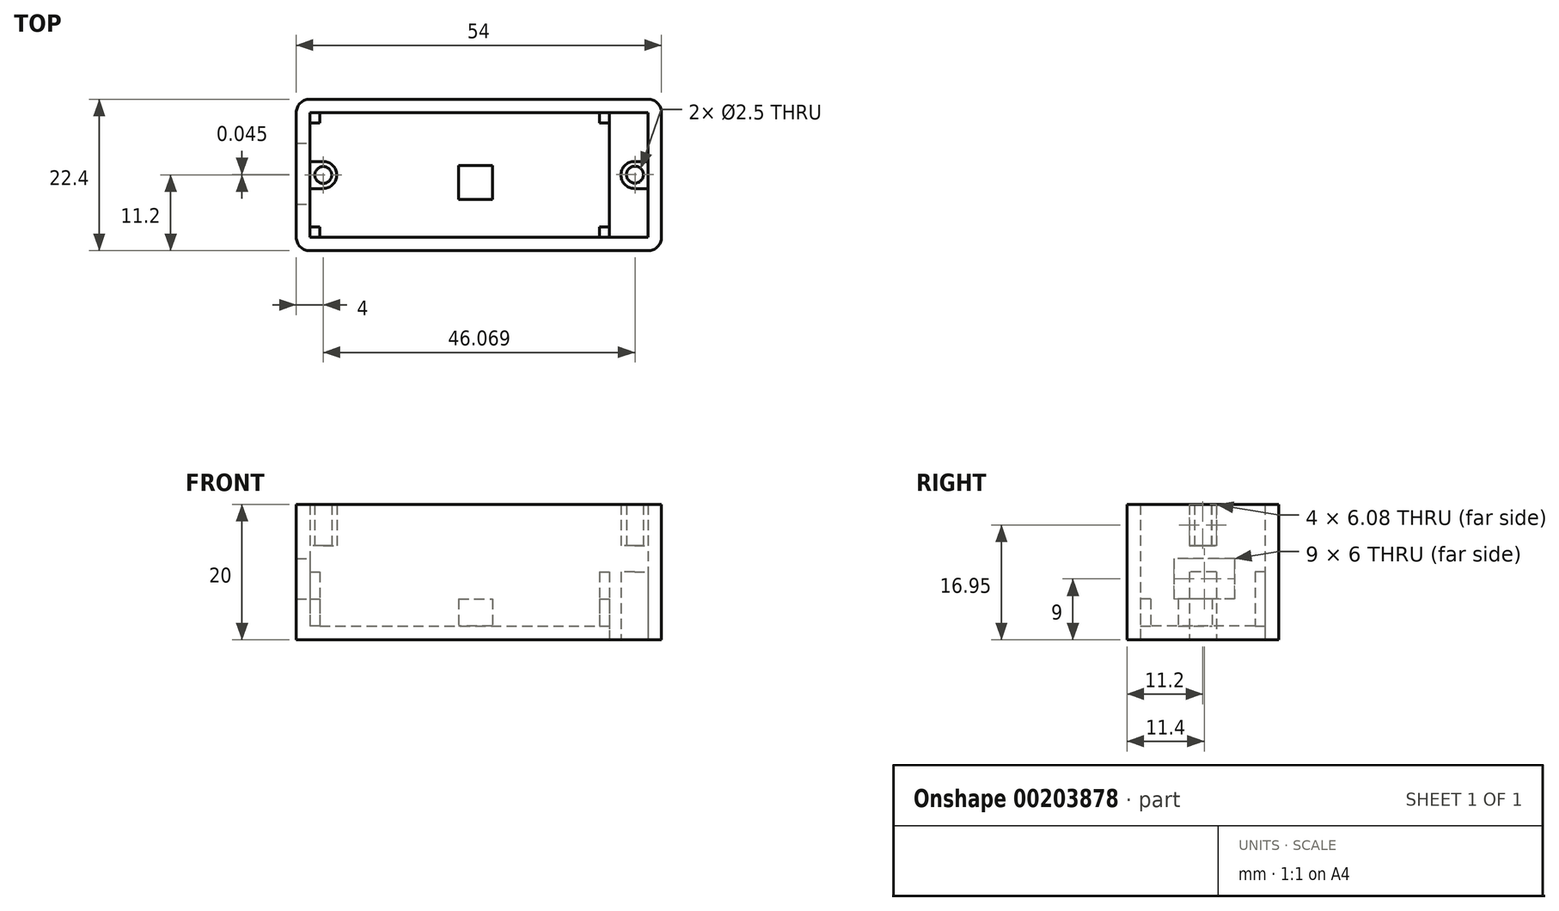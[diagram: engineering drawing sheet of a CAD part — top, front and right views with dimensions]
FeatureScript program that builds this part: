
annotation { "Feature Type Name" : "Feature", "Feature Type Description" : "" }
export const myFeature = defineFeature(function(context is Context, id is Id, definition is map)
    precondition{}
    {
        {
            var Q0;
            Q0=qCreatedBy(makeId("Top.planeOp"),FACE);
            var sketch = newSketch(context, id + "F0", { "sketchPlane" : qUnion([Q0])});
            skLineSegment(sketch, "E0.bottom", {"start": v(-31.58, 11.2) * mm, "end": v(22.42, 11.2) * mm});
            skLineSegment(sketch, "E0.top", {"start": v(-31.58, -11.2) * mm, "end": v(22.42, -11.2) * mm});
            skLineSegment(sketch, "E0.left", {"start": v(-31.58, 11.2) * mm, "end": v(-31.58, -11.2) * mm});
            skLineSegment(sketch, "E0.right", {"start": v(22.42, 11.2) * mm, "end": v(22.42, -11.2) * mm});
            skLineSegment(sketch, "E1.bottom", {"start": v(-29.58, 9.2) * mm, "end": v(20.42, 9.2) * mm});
            skLineSegment(sketch, "E1.top", {"start": v(-29.58, -9.2) * mm, "end": v(20.42, -9.2) * mm});
            skLineSegment(sketch, "E1.left", {"start": v(-29.58, 9.2) * mm, "end": v(-29.58, -9.2) * mm});
            skLineSegment(sketch, "E1.right", {"start": v(20.42, 9.2) * mm, "end": v(20.42, -9.2) * mm});
            skCircle(sketch, "E2", {"center": v(18.42, 0) * mm, "radius": 2 * mm});
            skCircle(sketch, "E3", {"center": v(-27.58, 0) * mm, "radius": 2 * mm});
            skLineSegment(sketch, "E4.bottom", {"start": v(-27.58, -2) * mm, "end": v(-29.58, -2) * mm});
            skLineSegment(sketch, "E4.top", {"start": v(-27.58, 2) * mm, "end": v(-29.58, 2) * mm});
            skLineSegment(sketch, "E4.left", {"start": v(-27.58, -2) * mm, "end": v(-27.58, 2) * mm});
            skLineSegment(sketch, "E4.right", {"start": v(-29.58, -2) * mm, "end": v(-29.58, 2) * mm});
            skLineSegment(sketch, "E5.bottom", {"start": v(18.42, 2) * mm, "end": v(20.42, 2) * mm});
            skLineSegment(sketch, "E5.top", {"start": v(18.42, -2) * mm, "end": v(20.42, -2) * mm});
            skLineSegment(sketch, "E5.left", {"start": v(18.42, 2) * mm, "end": v(18.42, -2) * mm});
            skLineSegment(sketch, "E5.right", {"start": v(20.42, 2) * mm, "end": v(20.42, -2) * mm});
            skCircle(sketch, "E6", {"center": v(-27.58, 0) * mm, "radius": 1.25 * mm});
            skCircle(sketch, "E7", {"center": v(18.49, 0.05) * mm, "radius": 1.25 * mm});
            skLineSegment(sketch, "E8.bottom", {"start": v(-29.58, 9.2) * mm, "end": v(14.72, 9.2) * mm});
            skLineSegment(sketch, "E8.top", {"start": v(-29.58, -9.2) * mm, "end": v(14.72, -9.2) * mm});
            skLineSegment(sketch, "E8.right", {"start": v(14.72, 9.2) * mm, "end": v(14.72, -9.2) * mm});
            skLineSegment(sketch, "E9.bottom", {"start": v(-7.58, 1.37) * mm, "end": v(-2.58, 1.37) * mm});
            skLineSegment(sketch, "E9.top", {"start": v(-7.58, -3.63) * mm, "end": v(-2.58, -3.63) * mm});
            skLineSegment(sketch, "E9.left", {"start": v(-7.58, 1.37) * mm, "end": v(-7.58, -3.63) * mm});
            skLineSegment(sketch, "E9.right", {"start": v(-2.58, 1.37) * mm, "end": v(-2.58, -3.63) * mm});
            skLineSegment(sketch, "E10.bottom", {"start": v(-28.08, 9.2) * mm, "end": v(-29.58, 9.2) * mm});
            skLineSegment(sketch, "E10.top", {"start": v(-28.08, 7.7) * mm, "end": v(-29.58, 7.7) * mm});
            skLineSegment(sketch, "E10.left", {"start": v(-28.08, 9.2) * mm, "end": v(-28.08, 7.7) * mm});
            skLineSegment(sketch, "E10.right", {"start": v(-29.58, 9.2) * mm, "end": v(-29.58, 7.7) * mm});
            skLineSegment(sketch, "E11.bottom", {"start": v(-29.58, -7.7) * mm, "end": v(-28.08, -7.7) * mm});
            skLineSegment(sketch, "E11.top", {"start": v(-29.58, -9.2) * mm, "end": v(-28.08, -9.2) * mm});
            skLineSegment(sketch, "E11.left", {"start": v(-29.58, -7.7) * mm, "end": v(-29.58, -9.2) * mm});
            skLineSegment(sketch, "E11.right", {"start": v(-28.08, -7.7) * mm, "end": v(-28.08, -9.2) * mm});
            skLineSegment(sketch, "E12.bottom", {"start": v(13.22, 9.2) * mm, "end": v(14.72, 9.2) * mm});
            skLineSegment(sketch, "E12.top", {"start": v(13.22, 7.7) * mm, "end": v(14.72, 7.7) * mm});
            skLineSegment(sketch, "E12.left", {"start": v(13.22, 9.2) * mm, "end": v(13.22, 7.7) * mm});
            skLineSegment(sketch, "E12.right", {"start": v(14.72, 9.2) * mm, "end": v(14.72, 7.7) * mm});
            skLineSegment(sketch, "E13.bottom", {"start": v(14.72, -7.7) * mm, "end": v(13.22, -7.7) * mm});
            skLineSegment(sketch, "E13.top", {"start": v(14.72, -9.2) * mm, "end": v(13.22, -9.2) * mm});
            skLineSegment(sketch, "E13.left", {"start": v(14.72, -7.7) * mm, "end": v(14.72, -9.2) * mm});
            skLineSegment(sketch, "E13.right", {"start": v(13.22, -7.7) * mm, "end": v(13.22, -9.2) * mm});
            skSolve(sketch);
        }
        {
            var Q0;
            Q0 = qSketchRegion(id + "F0", true);
            extrude(context, id + "F1", {"entities" : qUnion([Q0]), "depth" : 20 * mm});
        }
        {
            var Q0;
            Q0=makeQuery(id+"F0.imprint","IMPRINT",FACE,{"disambiguationData":[TD([[makeQuery(id+"F0.imprint","IMPRINT",EDGE,{"derivedFrom":sQuery(id+"F0.wireOp",EDGE,"E1.bottom")}),-1.0]])]});
            var Q1;
            {var subQ2=sQuery(id+"F0.wireOp",EDGE,"E4.bottom");Q1=makeQuery(id+"F0.imprint","IMPRINT",FACE,{"disambiguationData":[TD([[makeQuery(id+"F0.imprint","IMPRINT",EDGE,{"derivedFrom":subQ2}),1.0]])]});}
            var Q2;
            {var subQ0=sQuery(id+"F0.wireOp",EDGE,"E5.left");var subQ3=sQuery(id+"F0.wireOp",EDGE,"E7");var subQ5=makeQuery(id+"F0.imprint","INTERSECT",VERTEX,{"disambiguationData":[OD(0.0)],"derivedFrom":[subQ0,subQ3]});Q2=makeQuery(id+"F0.imprint","IMPRINT",FACE,{"disambiguationData":[TD([[makeQuery(id+"F0.imprint","IMPRINT",EDGE,{"disambiguationData":[TD([[subQ5,1.0]])],"derivedFrom":subQ3}),-1.0]])]});}
            var Q3;
            {var subQ0=sQuery(id+"F0.wireOp",EDGE,"E5.bottom");Q3=makeQuery(id+"F0.imprint","IMPRINT",FACE,{"disambiguationData":[TD([[makeQuery(id+"F0.imprint","IMPRINT",EDGE,{"derivedFrom":subQ0}),-1.0]])]});}
            var Q4;
            {var subQ0=sQuery(id+"F0.wireOp",EDGE,"E5.top");Q4=makeQuery(id+"F0.imprint","IMPRINT",FACE,{"disambiguationData":[TD([[makeQuery(id+"F0.imprint","IMPRINT",EDGE,{"derivedFrom":subQ0}),1.0]])]});}
            var Q5;
            {var subQ0=sQuery(id+"F0.wireOp",EDGE,"E5.left");var subQ4=sQuery(id+"F0.wireOp",EDGE,"E7");var subQ5=makeQuery(id+"F0.imprint","INTERSECT",VERTEX,{"disambiguationData":[OD(0.0)],"derivedFrom":[subQ0,subQ4]});Q5=makeQuery(id+"F0.imprint","IMPRINT",FACE,{"disambiguationData":[TD([[makeQuery(id+"F0.imprint","IMPRINT",EDGE,{"disambiguationData":[TD([[subQ5,-1.0]])],"derivedFrom":subQ4}),-1.0]])]});}
            var Q6;
            {var subQ0=sQuery(id+"F0.wireOp",EDGE,"E7");var subQ1=sQuery(id+"F0.wireOp",EDGE,"E5.left");var subQ2=makeQuery(id+"F0.imprint","INTERSECT",VERTEX,{"disambiguationData":[OD(0.0)],"derivedFrom":[subQ1,subQ0]});Q6=makeQuery(id+"F0.imprint","IMPRINT",FACE,{"disambiguationData":[TD([[makeQuery(id+"F0.imprint","IMPRINT",EDGE,{"disambiguationData":[TD([[subQ2,-1.0]])],"derivedFrom":subQ1}),-1.0]])]});}
            var Q7;
            {var subQ0=sQuery(id+"F0.wireOp",EDGE,"E7");var subQ1=sQuery(id+"F0.wireOp",EDGE,"E5.left");var subQ2=makeQuery(id+"F0.imprint","INTERSECT",VERTEX,{"disambiguationData":[OD(0.0)],"derivedFrom":[subQ1,subQ0]});Q7=makeQuery(id+"F0.imprint","IMPRINT",FACE,{"disambiguationData":[TD([[makeQuery(id+"F0.imprint","IMPRINT",EDGE,{"disambiguationData":[TD([[subQ2,-1.0]])],"derivedFrom":subQ1}),1.0]])]});}
            var Q8;
            {var subQ0=sQuery(id+"F0.wireOp",EDGE,"E4.top");Q8=makeQuery(id+"F0.imprint","IMPRINT",FACE,{"disambiguationData":[TD([[makeQuery(id+"F0.imprint","IMPRINT",EDGE,{"derivedFrom":subQ0}),1.0]])]});}
            var Q9;
            {var subQ0=sQuery(id+"F0.wireOp",EDGE,"E4.bottom");Q9=makeQuery(id+"F0.imprint","IMPRINT",FACE,{"disambiguationData":[TD([[makeQuery(id+"F0.imprint","IMPRINT",EDGE,{"derivedFrom":subQ0}),-1.0]])]});}
            var Q10;
            {var subQ0=sQuery(id+"F0.wireOp",EDGE,"E4.left");var subQ3=sQuery(id+"F0.wireOp",EDGE,"E6");var subQ6=makeQuery(id+"F0.imprint","INTERSECT",VERTEX,{"disambiguationData":[OD(0.0)],"derivedFrom":[subQ0,subQ3]});Q10=makeQuery(id+"F0.imprint","IMPRINT",FACE,{"disambiguationData":[TD([[makeQuery(id+"F0.imprint","IMPRINT",EDGE,{"disambiguationData":[TD([[subQ6,1.0]])],"derivedFrom":subQ3}),-1.0]])]});}
            var Q11;
            {var subQ0=sQuery(id+"F0.wireOp",EDGE,"E4.left");var subQ4=sQuery(id+"F0.wireOp",EDGE,"E6");var subQ5=makeQuery(id+"F0.imprint","INTERSECT",VERTEX,{"disambiguationData":[OD(0.0)],"derivedFrom":[subQ0,subQ4]});Q11=makeQuery(id+"F0.imprint","IMPRINT",FACE,{"disambiguationData":[TD([[makeQuery(id+"F0.imprint","IMPRINT",EDGE,{"disambiguationData":[TD([[subQ5,-1.0]])],"derivedFrom":subQ4}),-1.0]])]});}
            var Q12;
            {var subQ0=sQuery(id+"F0.wireOp",EDGE,"E6");var subQ1=sQuery(id+"F0.wireOp",EDGE,"E4.left");var subQ2=makeQuery(id+"F0.imprint","INTERSECT",VERTEX,{"disambiguationData":[OD(0.0)],"derivedFrom":[subQ1,subQ0]});Q12=makeQuery(id+"F0.imprint","IMPRINT",FACE,{"disambiguationData":[TD([[makeQuery(id+"F0.imprint","IMPRINT",EDGE,{"disambiguationData":[TD([[subQ2,-1.0]])],"derivedFrom":subQ1}),-1.0]])]});}
            var Q13;
            {var subQ0=sQuery(id+"F0.wireOp",EDGE,"E6");var subQ1=sQuery(id+"F0.wireOp",EDGE,"E4.left");var subQ2=makeQuery(id+"F0.imprint","INTERSECT",VERTEX,{"disambiguationData":[OD(0.0)],"derivedFrom":[subQ1,subQ0]});Q13=makeQuery(id+"F0.imprint","IMPRINT",FACE,{"disambiguationData":[TD([[makeQuery(id+"F0.imprint","IMPRINT",EDGE,{"disambiguationData":[TD([[subQ2,-1.0]])],"derivedFrom":subQ1}),1.0]])]});}
            var Q14;
            Q14=makeQuery(id+"F0.imprint","IMPRINT",FACE,{"disambiguationData":[TD([[makeQuery(id+"F0.imprint","IMPRINT",EDGE,{"derivedFrom":sQuery(id+"F0.wireOp",EDGE,"E9.bottom")}),-1.0]])]});
            var Q15;
            Q15=makeQuery(id+"F0.imprint","IMPRINT",FACE,{"disambiguationData":[TD([[makeQuery(id+"F0.imprint","IMPRINT",EDGE,{"derivedFrom":sQuery(id+"F0.wireOp",EDGE,"E10.bottom")}),1.0]])]});
            var Q16;
            Q16=makeQuery(id+"F0.imprint","IMPRINT",FACE,{"disambiguationData":[TD([[makeQuery(id+"F0.imprint","IMPRINT",EDGE,{"derivedFrom":sQuery(id+"F0.wireOp",EDGE,"E11.bottom")}),-1.0]])]});
            var Q17;
            Q17=makeQuery(id+"F0.imprint","IMPRINT",FACE,{"disambiguationData":[TD([[makeQuery(id+"F0.imprint","IMPRINT",EDGE,{"derivedFrom":sQuery(id+"F0.wireOp",EDGE,"E12.bottom")}),-1.0]])]});
            var Q18;
            Q18=makeQuery(id+"F0.imprint","IMPRINT",FACE,{"disambiguationData":[TD([[makeQuery(id+"F0.imprint","IMPRINT",EDGE,{"derivedFrom":sQuery(id+"F0.wireOp",EDGE,"E13.bottom")}),1.0]])]});
            extrude(context, id + "F2", {"entities" : qUnion([Q0, Q1, Q2, Q3, Q4, Q5, Q6, Q7, Q8, Q9, Q10, Q11, Q12, Q13, Q14, Q15, Q16, Q17, Q18]), "operationType" : NewBodyOperationType.ADD, "depth" : 2 * mm});
        }
        {
            var Q0;
            Q0=qCreatedBy(makeId("Right.planeOp"),FACE);
            var sketch = newSketch(context, id + "F3", { "sketchPlane" : qUnion([Q0])});
            skLineSegment(sketch, "E14.bottom", {"start": v(4.7, 12) * mm, "end": v(-4.3, 12) * mm});
            skLineSegment(sketch, "E14.top", {"start": v(4.7, 6) * mm, "end": v(-4.3, 6) * mm});
            skLineSegment(sketch, "E14.left", {"start": v(4.7, 12) * mm, "end": v(4.7, 6) * mm});
            skLineSegment(sketch, "E14.right", {"start": v(-4.3, 12) * mm, "end": v(-4.3, 6) * mm});
            skSolve(sketch);
        }
        {
            var Q0;
            Q0=makeQuery(id+"F3.imprint","IMPRINT",FACE,{"disambiguationData":[TD([[makeQuery(id+"F3.imprint","IMPRINT",EDGE,{"derivedFrom":sQuery(id+"F3.wireOp",EDGE,"E14.bottom")}),1.0]])]});
            extrude(context, id + "F4", {"entities" : qUnion([Q0]), "operationType" : NewBodyOperationType.REMOVE, "oppositeDirection" : true, "depth" : 35.8 * mm, "hasSecondDirection" : true, "secondDirectionOppositeDirection" : true, "secondDirectionDepth" : 20.2 * mm});
        }
        {
            var Q0;
            {var subQ0=sQuery(id+"F0.wireOp",EDGE,"E5.left");var subQ4=sQuery(id+"F0.wireOp",EDGE,"E7");var subQ5=makeQuery(id+"F0.imprint","INTERSECT",VERTEX,{"disambiguationData":[OD(0.0)],"derivedFrom":[subQ0,subQ4]});Q0=makeQuery(id+"F0.imprint","IMPRINT",FACE,{"disambiguationData":[TD([[makeQuery(id+"F0.imprint","IMPRINT",EDGE,{"disambiguationData":[TD([[subQ5,-1.0]])],"derivedFrom":subQ4}),-1.0]])]});}
            var Q1;
            {var subQ0=sQuery(id+"F0.wireOp",EDGE,"E7");var subQ1=sQuery(id+"F0.wireOp",EDGE,"E5.left");var subQ2=makeQuery(id+"F0.imprint","INTERSECT",VERTEX,{"disambiguationData":[OD(0.0)],"derivedFrom":[subQ1,subQ0]});Q1=makeQuery(id+"F0.imprint","IMPRINT",FACE,{"disambiguationData":[TD([[makeQuery(id+"F0.imprint","IMPRINT",EDGE,{"disambiguationData":[TD([[subQ2,-1.0]])],"derivedFrom":subQ1}),-1.0]])]});}
            var Q2;
            {var subQ0=sQuery(id+"F0.wireOp",EDGE,"E7");var subQ1=sQuery(id+"F0.wireOp",EDGE,"E5.left");var subQ2=makeQuery(id+"F0.imprint","INTERSECT",VERTEX,{"disambiguationData":[OD(0.0)],"derivedFrom":[subQ1,subQ0]});Q2=makeQuery(id+"F0.imprint","IMPRINT",FACE,{"disambiguationData":[TD([[makeQuery(id+"F0.imprint","IMPRINT",EDGE,{"disambiguationData":[TD([[subQ2,-1.0]])],"derivedFrom":subQ1}),1.0]])]});}
            var Q3;
            {var subQ0=sQuery(id+"F0.wireOp",EDGE,"E5.left");var subQ3=sQuery(id+"F0.wireOp",EDGE,"E7");var subQ5=makeQuery(id+"F0.imprint","INTERSECT",VERTEX,{"disambiguationData":[OD(0.0)],"derivedFrom":[subQ0,subQ3]});Q3=makeQuery(id+"F0.imprint","IMPRINT",FACE,{"disambiguationData":[TD([[makeQuery(id+"F0.imprint","IMPRINT",EDGE,{"disambiguationData":[TD([[subQ5,1.0]])],"derivedFrom":subQ3}),-1.0]])]});}
            var Q4;
            {var subQ0=sQuery(id+"F0.wireOp",EDGE,"E5.bottom");Q4=makeQuery(id+"F0.imprint","IMPRINT",FACE,{"disambiguationData":[TD([[makeQuery(id+"F0.imprint","IMPRINT",EDGE,{"derivedFrom":subQ0}),-1.0]])]});}
            var Q5;
            {var subQ0=sQuery(id+"F0.wireOp",EDGE,"E5.top");Q5=makeQuery(id+"F0.imprint","IMPRINT",FACE,{"disambiguationData":[TD([[makeQuery(id+"F0.imprint","IMPRINT",EDGE,{"derivedFrom":subQ0}),1.0]])]});}
            var Q6;
            {var subQ4=sQuery(id+"F0.wireOp",EDGE,"E1.bottom");Q6=makeQuery(id+"F0.imprint","IMPRINT",FACE,{"disambiguationData":[TD([[makeQuery(id+"F0.imprint","IMPRINT",EDGE,{"derivedFrom":subQ4}),-1.0]])]});}
            extrude(context, id + "F5", {"entities" : qUnion([Q0, Q1, Q2, Q3, Q4, Q5, Q6]), "operationType" : NewBodyOperationType.ADD, "depth" : 10 * mm});
        }
        {
            var Q0;
            {var subQ0=sQuery(id+"F0.wireOp",EDGE,"E5.bottom");Q0=makeQuery(id+"F0.imprint","IMPRINT",FACE,{"disambiguationData":[TD([[makeQuery(id+"F0.imprint","IMPRINT",EDGE,{"derivedFrom":subQ0}),-1.0]])]});}
            var Q1;
            {var subQ0=sQuery(id+"F0.wireOp",EDGE,"E5.left");var subQ3=sQuery(id+"F0.wireOp",EDGE,"E7");var subQ5=makeQuery(id+"F0.imprint","INTERSECT",VERTEX,{"disambiguationData":[OD(0.0)],"derivedFrom":[subQ0,subQ3]});Q1=makeQuery(id+"F0.imprint","IMPRINT",FACE,{"disambiguationData":[TD([[makeQuery(id+"F0.imprint","IMPRINT",EDGE,{"disambiguationData":[TD([[subQ5,1.0]])],"derivedFrom":subQ3}),-1.0]])]});}
            var Q2;
            {var subQ0=sQuery(id+"F0.wireOp",EDGE,"E5.top");Q2=makeQuery(id+"F0.imprint","IMPRINT",FACE,{"disambiguationData":[TD([[makeQuery(id+"F0.imprint","IMPRINT",EDGE,{"derivedFrom":subQ0}),1.0]])]});}
            var Q3;
            {var subQ0=sQuery(id+"F0.wireOp",EDGE,"E5.left");var subQ4=sQuery(id+"F0.wireOp",EDGE,"E7");var subQ5=makeQuery(id+"F0.imprint","INTERSECT",VERTEX,{"disambiguationData":[OD(0.0)],"derivedFrom":[subQ0,subQ4]});Q3=makeQuery(id+"F0.imprint","IMPRINT",FACE,{"disambiguationData":[TD([[makeQuery(id+"F0.imprint","IMPRINT",EDGE,{"disambiguationData":[TD([[subQ5,-1.0]])],"derivedFrom":subQ4}),-1.0]])]});}
            var Q4;
            {var subQ0=sQuery(id+"F0.wireOp",EDGE,"E4.top");Q4=makeQuery(id+"F0.imprint","IMPRINT",FACE,{"disambiguationData":[TD([[makeQuery(id+"F0.imprint","IMPRINT",EDGE,{"derivedFrom":subQ0}),1.0]])]});}
            var Q5;
            {var subQ0=sQuery(id+"F0.wireOp",EDGE,"E4.left");var subQ3=sQuery(id+"F0.wireOp",EDGE,"E6");var subQ6=makeQuery(id+"F0.imprint","INTERSECT",VERTEX,{"disambiguationData":[OD(0.0)],"derivedFrom":[subQ0,subQ3]});Q5=makeQuery(id+"F0.imprint","IMPRINT",FACE,{"disambiguationData":[TD([[makeQuery(id+"F0.imprint","IMPRINT",EDGE,{"disambiguationData":[TD([[subQ6,1.0]])],"derivedFrom":subQ3}),-1.0]])]});}
            var Q6;
            {var subQ0=sQuery(id+"F0.wireOp",EDGE,"E4.left");var subQ4=sQuery(id+"F0.wireOp",EDGE,"E6");var subQ5=makeQuery(id+"F0.imprint","INTERSECT",VERTEX,{"disambiguationData":[OD(0.0)],"derivedFrom":[subQ0,subQ4]});Q6=makeQuery(id+"F0.imprint","IMPRINT",FACE,{"disambiguationData":[TD([[makeQuery(id+"F0.imprint","IMPRINT",EDGE,{"disambiguationData":[TD([[subQ5,-1.0]])],"derivedFrom":subQ4}),-1.0]])]});}
            var Q7;
            {var subQ0=sQuery(id+"F0.wireOp",EDGE,"E4.bottom");Q7=makeQuery(id+"F0.imprint","IMPRINT",FACE,{"disambiguationData":[TD([[makeQuery(id+"F0.imprint","IMPRINT",EDGE,{"derivedFrom":subQ0}),-1.0]])]});}
            extrude(context, id + "F6", {"entities" : qUnion([Q0, Q1, Q2, Q3, Q4, Q5, Q6, Q7]), "operationType" : NewBodyOperationType.ADD, "depth" : 20 * mm, "hasSecondDirection" : true, "secondDirectionOppositeDirection" : false, "secondDirectionDepth" : 13.9 * mm});
        }
        {
            var Q0;
            Q0=makeQuery(id+"F1.opExtrude","SWEPT_EDGE",EDGE,{"disambiguationData":[OSD([sQuery(id+"F0.wireOp",EDGE,"E0.top"),sQuery(id+"F0.wireOp",EDGE,"E0.left")])]});
            var Q1;
            Q1=makeQuery(id+"F1.opExtrude","SWEPT_EDGE",EDGE,{"disambiguationData":[OSD([sQuery(id+"F0.wireOp",EDGE,"E0.bottom"),sQuery(id+"F0.wireOp",EDGE,"E0.left")])]});
            var Q2;
            Q2=makeQuery(id+"F1.opExtrude","SWEPT_EDGE",EDGE,{"disambiguationData":[OSD([sQuery(id+"F0.wireOp",EDGE,"E0.bottom"),sQuery(id+"F0.wireOp",EDGE,"E0.right")])]});
            var Q3;
            Q3=makeQuery(id+"F6.opExtrude","SWEPT_EDGE",EDGE,{"disambiguationData":[OSD([sQuery(id+"F0.wireOp",EDGE,"E4.top"),sQuery(id+"F0.wireOp",EDGE,"E1.left")])]});
            var Q4;
            Q4=makeQuery(id+"F6.opExtrude","SWEPT_EDGE",EDGE,{"disambiguationData":[OSD([sQuery(id+"F0.wireOp",EDGE,"E4.bottom"),sQuery(id+"F0.wireOp",EDGE,"E1.left")])]});
            var Q5;
            Q5=makeQuery(id+"F6.opExtrude","SWEPT_EDGE",EDGE,{"disambiguationData":[OSD([sQuery(id+"F0.wireOp",EDGE,"E1.right"),sQuery(id+"F0.wireOp",EDGE,"E5.top"),sQuery(id+"F0.wireOp",EDGE,"E5.right")])]});
            var Q6;
            Q6=makeQuery(id+"F6.opExtrude","SWEPT_EDGE",EDGE,{"disambiguationData":[OSD([sQuery(id+"F0.wireOp",EDGE,"E1.right"),sQuery(id+"F0.wireOp",EDGE,"E5.bottom"),sQuery(id+"F0.wireOp",EDGE,"E5.right")])]});
            var Q7;
            Q7=makeQuery(id+"F1.opExtrude","SWEPT_EDGE",EDGE,{"disambiguationData":[OSD([sQuery(id+"F0.wireOp",EDGE,"E0.top"),sQuery(id+"F0.wireOp",EDGE,"E0.right")])]});
            fillet(context, id + "F7", {"entities" : qUnion([Q0, Q1, Q2, Q3, Q4, Q5, Q6, Q7]), "radius" : 2 * mm, "tangentPropagation" : true, "allowEdgeOverflow" : false});
        }
        {
            var Q0;
            Q0=makeQuery(id+"F0.imprint","IMPRINT",FACE,{"disambiguationData":[TD([[makeQuery(id+"F0.imprint","IMPRINT",EDGE,{"derivedFrom":sQuery(id+"F0.wireOp",EDGE,"E9.bottom")}),-1.0]])]});
            var Q1;
            Q1=makeQuery(id+"F0.imprint","IMPRINT",FACE,{"disambiguationData":[TD([[makeQuery(id+"F0.imprint","IMPRINT",EDGE,{"derivedFrom":sQuery(id+"F0.wireOp",EDGE,"E10.bottom")}),1.0]])]});
            var Q2;
            Q2=makeQuery(id+"F0.imprint","IMPRINT",FACE,{"disambiguationData":[TD([[makeQuery(id+"F0.imprint","IMPRINT",EDGE,{"derivedFrom":sQuery(id+"F0.wireOp",EDGE,"E11.bottom")}),-1.0]])]});
            var Q3;
            Q3=makeQuery(id+"F0.imprint","IMPRINT",FACE,{"disambiguationData":[TD([[makeQuery(id+"F0.imprint","IMPRINT",EDGE,{"derivedFrom":sQuery(id+"F0.wireOp",EDGE,"E12.bottom")}),-1.0]])]});
            var Q4;
            Q4=makeQuery(id+"F0.imprint","IMPRINT",FACE,{"disambiguationData":[TD([[makeQuery(id+"F0.imprint","IMPRINT",EDGE,{"derivedFrom":sQuery(id+"F0.wireOp",EDGE,"E13.bottom")}),1.0]])]});
            extrude(context, id + "F8", {"entities" : qUnion([Q0, Q1, Q2, Q3, Q4]), "operationType" : NewBodyOperationType.ADD, "depth" : 6 * mm});
        }
    });
